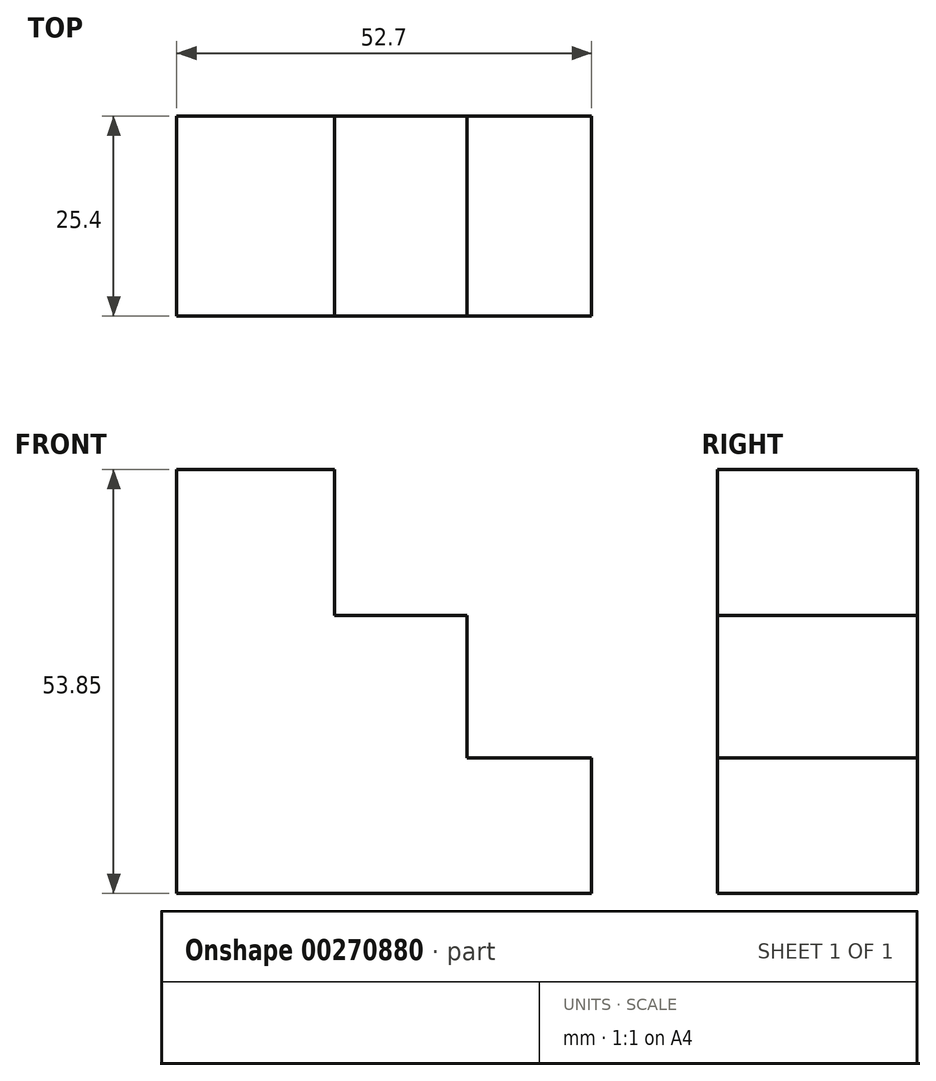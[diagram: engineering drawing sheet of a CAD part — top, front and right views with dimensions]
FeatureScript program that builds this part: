
annotation { "Feature Type Name" : "Feature", "Feature Type Description" : "" }
export const myFeature = defineFeature(function(context is Context, id is Id, definition is map)
    precondition{}
    {
        {
            var Q0;
            Q0=qCreatedBy(makeId("Front.planeOp"),FACE);
            var sketch = newSketch(context, id + "F0", { "sketchPlane" : qUnion([Q0])});
            skLineSegment(sketch, "E0.bottom", {"start": v(0, 0) * mm, "end": v(-52.7, 0) * mm});
            skLineSegment(sketch, "E0.top", {"start": v(0, 0) * mm, "end": v(-52.7, 0) * mm});
            skLineSegment(sketch, "E0.left", {"start": v(0, 0) * mm, "end": v(0, 0) * mm});
            skLineSegment(sketch, "E0.right", {"start": v(-52.7, 0) * mm, "end": v(-52.7, 0) * mm});
            skLineSegment(sketch, "E1.bottom", {"start": v(-52.7, 53.85) * mm, "end": v(-52.7, 53.85) * mm});
            skLineSegment(sketch, "E1.left", {"start": v(-52.7, 53.85) * mm, "end": v(-52.7, 0) * mm});
            skLineSegment(sketch, "E1.right", {"start": v(-52.7, 53.85) * mm, "end": v(-52.7, 0) * mm});
            skLineSegment(sketch, "E2.bottom", {"start": v(-52.7, 53.85) * mm, "end": v(-32.65, 53.85) * mm});
            skLineSegment(sketch, "E2.top", {"start": v(-52.7, 53.85) * mm, "end": v(-32.65, 53.85) * mm});
            skLineSegment(sketch, "E2.right", {"start": v(-32.65, 53.85) * mm, "end": v(-32.65, 53.85) * mm});
            skLineSegment(sketch, "E3.top", {"start": v(-32.65, 35.33) * mm, "end": v(-32.65, 35.33) * mm});
            skLineSegment(sketch, "E3.left", {"start": v(-32.65, 53.85) * mm, "end": v(-32.65, 35.33) * mm});
            skLineSegment(sketch, "E3.right", {"start": v(-32.65, 53.85) * mm, "end": v(-32.65, 35.33) * mm});
            skLineSegment(sketch, "E4.bottom", {"start": v(-32.65, 35.33) * mm, "end": v(-15.85, 35.33) * mm});
            skLineSegment(sketch, "E4.top", {"start": v(-32.65, 35.33) * mm, "end": v(-15.85, 35.33) * mm});
            skLineSegment(sketch, "E4.right", {"start": v(-15.85, 35.33) * mm, "end": v(-15.85, 35.33) * mm});
            skLineSegment(sketch, "E5.bottom", {"start": v(-15.85, 17.19) * mm, "end": v(-15.85, 17.19) * mm});
            skLineSegment(sketch, "E5.left", {"start": v(-15.85, 17.19) * mm, "end": v(-15.85, 35.33) * mm});
            skLineSegment(sketch, "E5.right", {"start": v(-15.85, 17.19) * mm, "end": v(-15.85, 35.33) * mm});
            skLineSegment(sketch, "E6.bottom", {"start": v(-15.85, 17.19) * mm, "end": v(0, 17.19) * mm});
            skLineSegment(sketch, "E6.top", {"start": v(-15.85, 17.19) * mm, "end": v(0, 17.19) * mm});
            skLineSegment(sketch, "E6.right", {"start": v(0, 17.19) * mm, "end": v(0, 17.19) * mm});
            skLineSegment(sketch, "E7.left", {"start": v(0, 0) * mm, "end": v(0, 17.19) * mm});
            skLineSegment(sketch, "E7.right", {"start": v(0, 0) * mm, "end": v(0, 17.19) * mm});
            skSolve(sketch);
        }
        {
            var Q0;
            Q0 = qSketchRegion(id + "F0", true);
            extrude(context, id + "F1", {"entities" : qUnion([Q0]), "depth" : 25.4 * mm});
        }
    });
